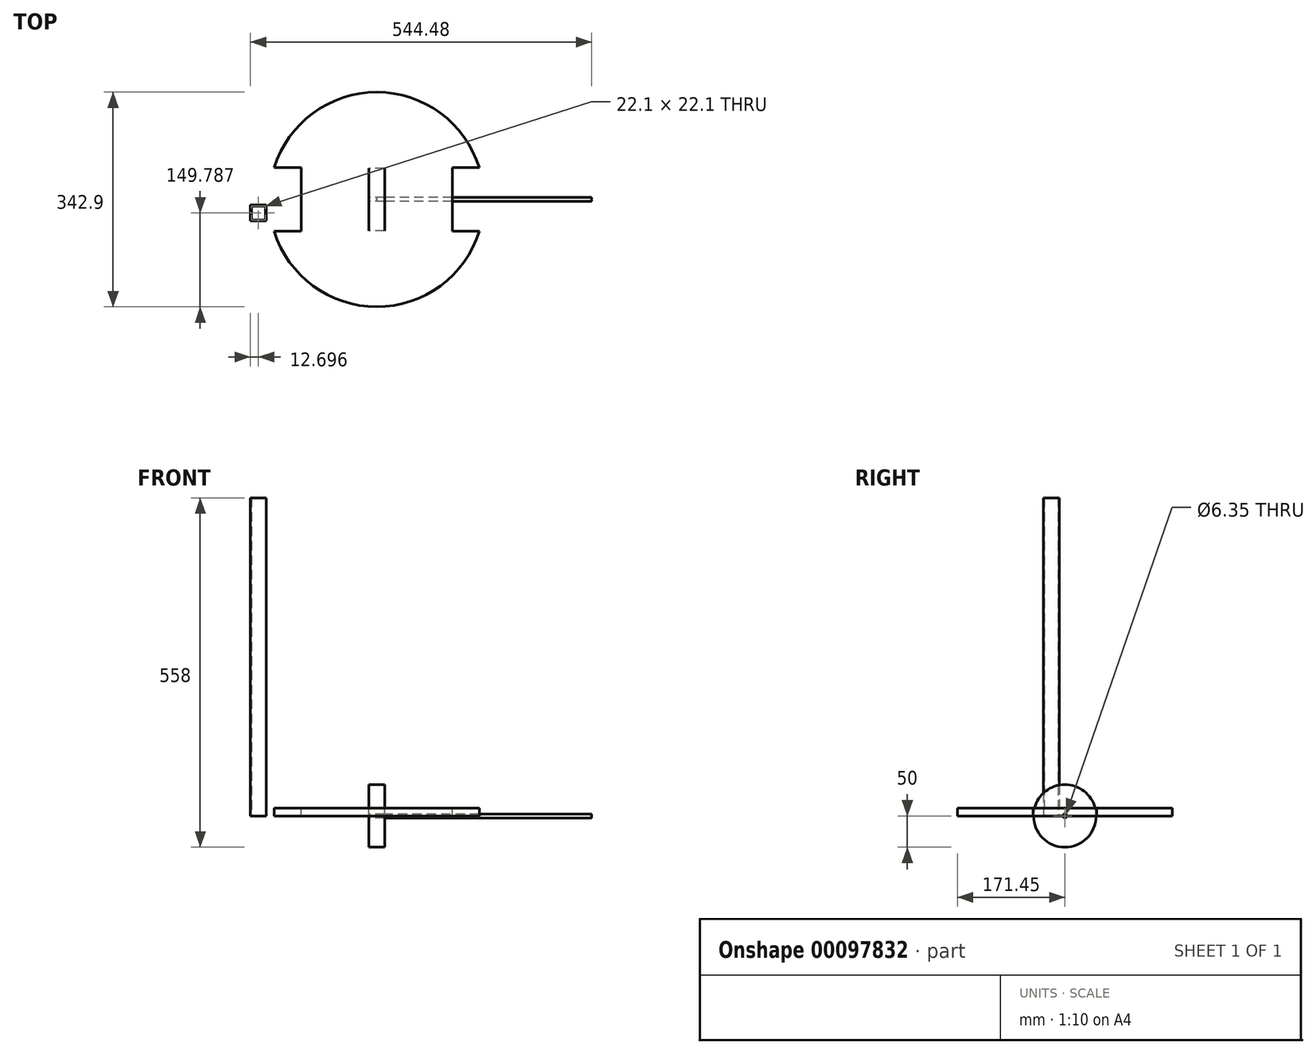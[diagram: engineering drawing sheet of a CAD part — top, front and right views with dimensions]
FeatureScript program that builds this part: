
annotation { "Feature Type Name" : "Feature", "Feature Type Description" : "" }
export const myFeature = defineFeature(function(context is Context, id is Id, definition is map)
    precondition{}
    {
        {
            var Q0;
            Q0=qCreatedBy(makeId("Top.planeOp"),FACE);
            var sketch = newSketch(context, id + "F0", { "sketchPlane" : qUnion([Q0])});
            skCircle(sketch, "E0", {"center": v(0, 0) * mm, "radius": 171.45 * mm});
            skSolve(sketch);
        }
        {
            var Q0;
            Q0 = qSketchRegion(id + "F0", true);
            extrude(context, id + "F1", {"entities" : qUnion([Q0]), "depth" : 12.7 * mm});
        }
        {
            var Q0;
            Q0=makeQuery(id+"F1.opExtrude","CAP_FACE",FACE,{"disambiguationData":[OSD([sQuery(id+"F0.wireOp",EDGE,"E0")])],"isStart":false});
            var sketch = newSketch(context, id + "F2", { "sketchPlane" : qUnion([Q0])});
            skLineSegment(sketch, "E1.bottom", {"start": v(-171.45, 50.8) * mm, "end": v(-120.65, 50.8) * mm});
            skLineSegment(sketch, "E1.top", {"start": v(-171.45, -50.8) * mm, "end": v(-120.65, -50.8) * mm});
            skLineSegment(sketch, "E1.left", {"start": v(-171.45, 50.8) * mm, "end": v(-171.45, -50.8) * mm});
            skLineSegment(sketch, "E1.right", {"start": v(-120.65, 50.8) * mm, "end": v(-120.65, -50.8) * mm});
            skLineSegment(sketch, "E2.bottom", {"start": v(120.65, 50.8) * mm, "end": v(171.45, 50.8) * mm});
            skLineSegment(sketch, "E2.top", {"start": v(120.65, -50.8) * mm, "end": v(171.45, -50.8) * mm});
            skLineSegment(sketch, "E2.left", {"start": v(120.65, 50.8) * mm, "end": v(120.65, -50.8) * mm});
            skLineSegment(sketch, "E2.right", {"start": v(171.45, 50.8) * mm, "end": v(171.45, -50.8) * mm});
            skLineSegment(sketch, "E3", {"start": v(-120.65, 0) * mm, "end": v(120.65, 0) * mm, "construction": true});
            skSolve(sketch);
        }
        {
            var Q0;
            Q0 = qSketchRegion(id + "F2", true);
            extrude(context, id + "F3", {"entities" : qUnion([Q0]), "operationType" : NewBodyOperationType.REMOVE, "endBound" : BoundingType.THROUGH_ALL, "oppositeDirection" : true, "depth" : 25.4 * mm});
        }
        {
            var Q0;
            Q0=qCreatedBy(makeId("Front.planeOp"),FACE);
            var sketch = newSketch(context, id + "F4", { "sketchPlane" : qUnion([Q0])});
            skLineSegment(sketch, "E4", {"start": v(-14.08, 0) * mm, "end": v(18.79, 0) * mm, "construction": true});
            skLineSegment(sketch, "E5", {"start": v(0, 3.18) * mm, "end": v(0, 0) * mm, "construction": true});
            skLineSegment(sketch, "E6.bottom", {"start": v(-12.7, 50) * mm, "end": v(12.7, 50) * mm});
            skLineSegment(sketch, "E6.top", {"start": v(-12.7, 3.18) * mm, "end": v(12.7, 3.18) * mm});
            skLineSegment(sketch, "E6.left", {"start": v(-12.7, 50) * mm, "end": v(-12.7, 3.18) * mm});
            skLineSegment(sketch, "E6.right", {"start": v(12.7, 50) * mm, "end": v(12.7, 3.18) * mm});
            skSolve(sketch);
        }
        {
            var Q0;
            Q0 = qSketchRegion(id + "F4", true);
            var Q1;
            Q1=sQuery(id+"F4.wireOp",EDGE,"E4");
            revolve(context, id + "F5", {"entities" : qUnion([Q0]), "axis" : qUnion([Q1]), "revolveType" : RevolveType.FULL});
        }
        {
            var Q0;
            Q0=qCreatedBy(makeId("Right.planeOp"),FACE);
            var sketch = newSketch(context, id + "F6", { "sketchPlane" : qUnion([Q0])});
            skCircle(sketch, "E7", {"center": v(0, 0) * mm, "radius": 3.18 * mm});
            skSolve(sketch);
        }
        {
            var Q0;
            Q0 = qSketchRegion(id + "F6", true);
            var Q1;
            Q1 = qConstructionFilter(qBodyType(qCreatedBy(id + "F6" ,EDGE), BodyType.WIRE), ConstructionObject.NO);
            extrude(context, id + "F7", {"entities" : qUnion([Q0]), "surfaceEntities" : qUnion([Q1]), "depth" : 342.9 * mm});
        }
        {
            var Q0;
            Q0=qCreatedBy(makeId("Top.planeOp"),FACE);
            var sketch = newSketch(context, id + "F8", { "sketchPlane" : qUnion([Q0])});
            skLineSegment(sketch, "E8.bottom", {"start": v(-201.58, -8.96) * mm, "end": v(-176.18, -8.96) * mm});
            skLineSegment(sketch, "E8.top", {"start": v(-201.58, -34.36) * mm, "end": v(-176.18, -34.36) * mm});
            skLineSegment(sketch, "E8.left", {"start": v(-201.58, -8.96) * mm, "end": v(-201.58, -34.36) * mm});
            skLineSegment(sketch, "E8.right", {"start": v(-176.18, -8.96) * mm, "end": v(-176.18, -34.36) * mm});
            skLineSegment(sketch, "E9.bottom", {"start": v(-199.93, -32.71) * mm, "end": v(-177.84, -32.71) * mm});
            skLineSegment(sketch, "E9.top", {"start": v(-199.93, -10.61) * mm, "end": v(-177.84, -10.61) * mm});
            skLineSegment(sketch, "E9.left", {"start": v(-199.93, -32.71) * mm, "end": v(-199.93, -10.61) * mm});
            skLineSegment(sketch, "E9.right", {"start": v(-177.84, -32.71) * mm, "end": v(-177.84, -10.61) * mm});
            skSolve(sketch);
        }
        {
            var Q0;
            Q0=makeQuery(id+"F8.imprint","IMPRINT",FACE,{"disambiguationData":[TD([[makeQuery(id+"F8.imprint","IMPRINT",EDGE,{"derivedFrom":sQuery(id+"F8.wireOp",EDGE,"E8.bottom")}),-1.0]])]});
            extrude(context, id + "F9", {"entities" : qUnion([Q0]), "depth" : 508 * mm});
        }
    });
